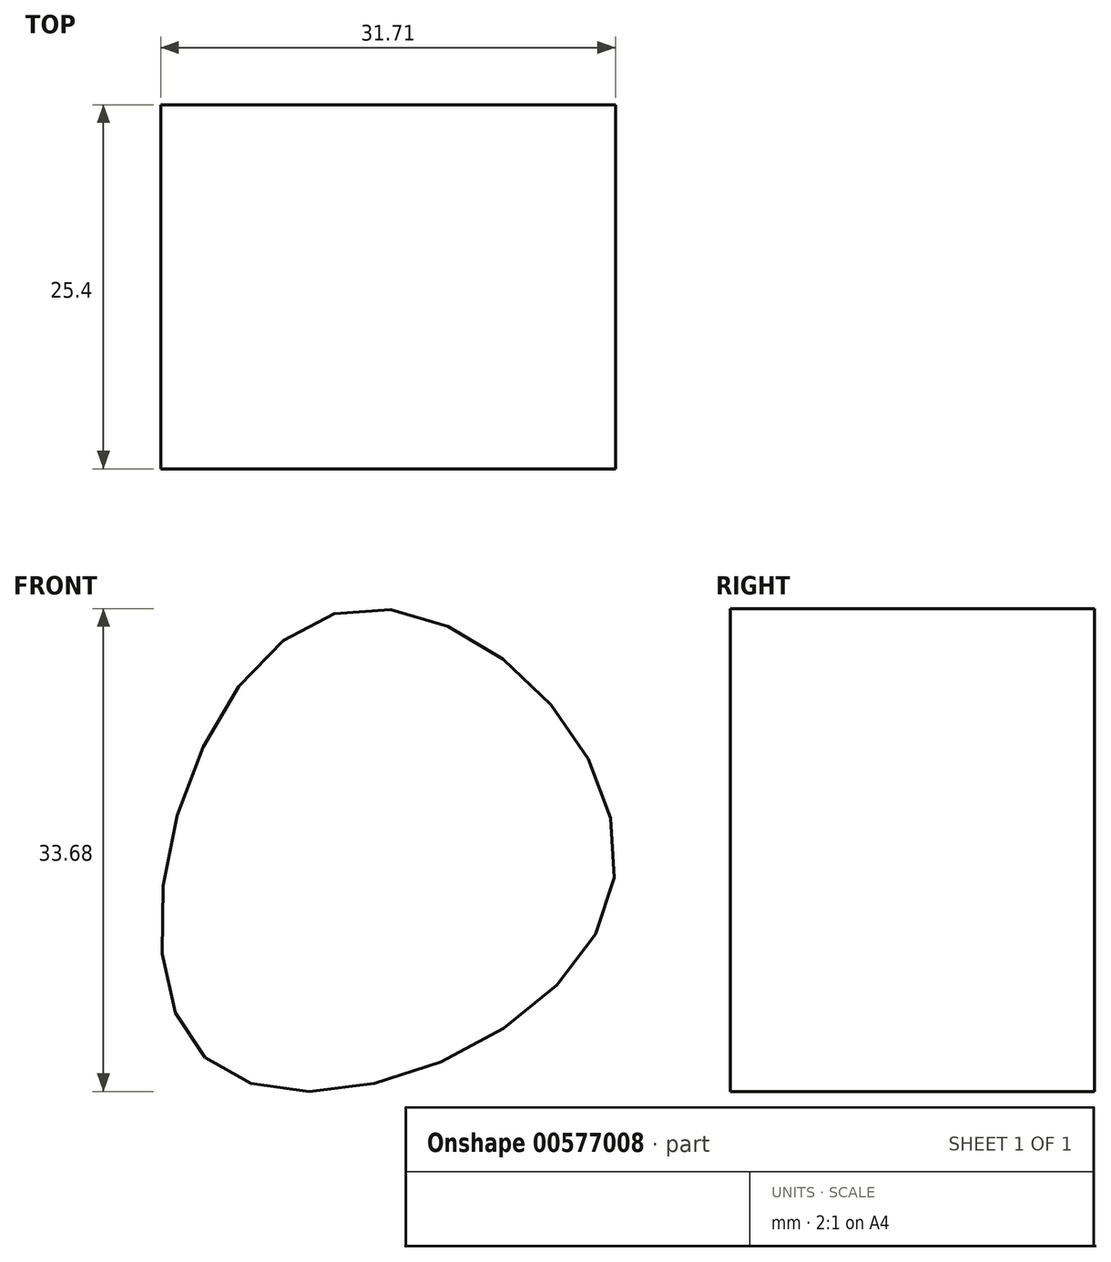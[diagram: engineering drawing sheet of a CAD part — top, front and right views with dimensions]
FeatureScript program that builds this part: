
annotation { "Feature Type Name" : "Feature", "Feature Type Description" : "" }
export const myFeature = defineFeature(function(context is Context, id is Id, definition is map)
    precondition{}
    {
        {
            var Q0;
            Q0=qCreatedBy(makeId("Front.planeOp"),FACE);
            var sketch = newSketch(context, id + "F0", { "sketchPlane" : qUnion([Q0])});
            skFitSpline(sketch, "E0", {"points": [v(-12.02, -13.9) * mm, v(-3.3, 16.96) * mm, v(16.33, -2.45) * mm, v(-12.02, -13.9) * mm]});
            skSolve(sketch);
        }
        {
            var Q0;
            Q0 = qSketchRegion(id + "F0", true);
            extrude(context, id + "F1", {"entities" : qUnion([Q0]), "depth" : 25.4 * mm, "offsetDistance" : 25.4 * mm});
        }
    });
